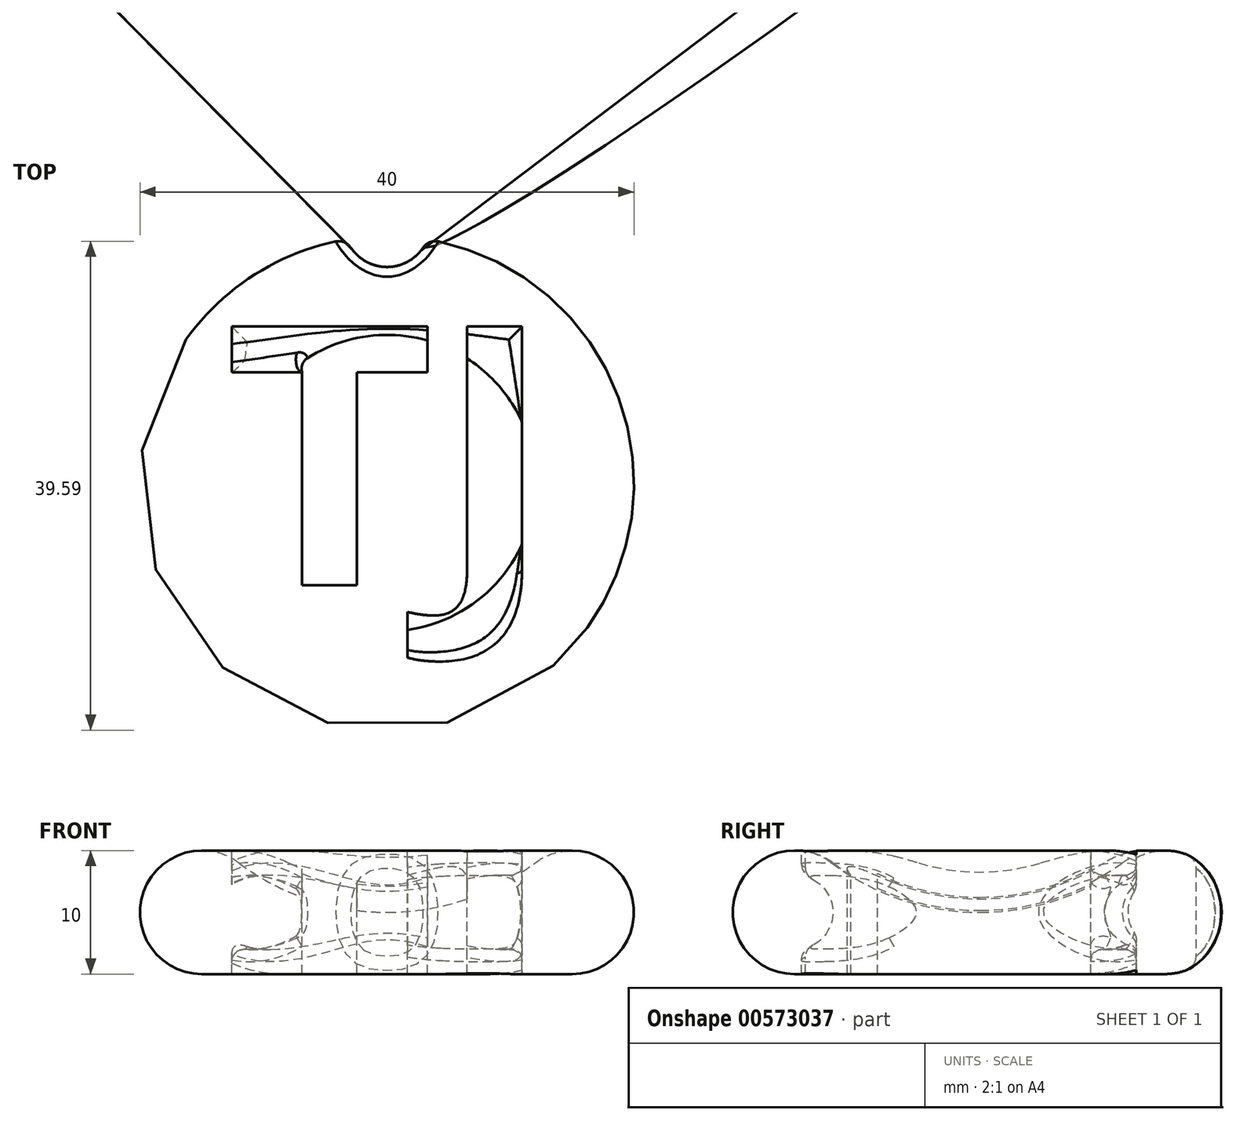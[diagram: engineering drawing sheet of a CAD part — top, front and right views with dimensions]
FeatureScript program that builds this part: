
annotation { "Feature Type Name" : "Feature", "Feature Type Description" : "" }
export const myFeature = defineFeature(function(context is Context, id is Id, definition is map)
    precondition{}
    {
        {
            var Q0;
            Q0=qCreatedBy(makeId("Front.planeOp"),FACE);
            var sketch = newSketch(context, id + "F0", { "sketchPlane" : qUnion([Q0])});
            skArc(sketch, "E0", {"start": v(-12, 9) * mm, "mid": v(-19.74, 6.58) * mm, "end": v(-15, 0) * mm});
            skArc(sketch, "E1", {"start": v(-12, 9) * mm, "mid": v(-6.32, 6.03) * mm, "end": v(0, 5) * mm});
            skLineSegment(sketch, "E2", {"start": v(0, 0) * mm, "end": v(-15, 0) * mm});
            skLineSegment(sketch, "E3", {"start": v(0, 0) * mm, "end": v(0, 5) * mm});
            skSolve(sketch);
        }
        {
            var Q0;
            Q0=makeQuery(id+"F0.imprint","IMPRINT",FACE,{"disambiguationData":[TD([[makeQuery(id+"F0.imprint","IMPRINT",EDGE,{"derivedFrom":sQuery(id+"F0.wireOp",EDGE,"E0")}),1.0]])]});
            var Q1;
            Q1=sQuery(id+"F0.wireOp",EDGE,"E3");
            revolve(context, id + "F1", {"entities" : qUnion([Q0]), "axis" : qUnion([Q1]), "revolveType" : RevolveType.FULL});
        }
        {
            var Q0;
            Q0=qCreatedBy(makeId("Top.planeOp"),FACE);
            cPlane(context, id + "F2", {"entities" : qUnion([Q0]), "cplaneType" : CPlaneType.OFFSET, "offset" : 11 * mm, "width" : 150 * mm, "height" : 150 * mm});
        }
        {
            var Q0;
            Q0=qCreatedBy(id+"F2.planeOp",FACE);
            var sketch = newSketch(context, id + "F3", { "sketchPlane" : qUnion([Q0])});
            skText(sketch, "E4", { "text": "TJ", "fontName": "OpenSans-Bold.ttf"});
            const initialGuessF3  = {"E4": [-0.01315, -0.00828, 1, 0, 0.02114]};
            skSetInitialGuess(sketch, initialGuessF3);
            skSolve(sketch);
        }
        {
            var Q0;
            Q0=makeQuery(id+"F3.imprint","IMPRINT",FACE,{"disambiguationData":[TD([[makeQuery(id+"F3.imprint","IMPRINT",EDGE,{"derivedFrom":sQuery(id+"F3.wireOp",EDGE,"E4.sketch_text.stroke-0")}),-1.0]])]});
            var Q1;
            Q1=makeQuery(id+"F3.imprint","IMPRINT",FACE,{"disambiguationData":[TD([[makeQuery(id+"F3.imprint","IMPRINT",EDGE,{"derivedFrom":sQuery(id+"F3.wireOp",EDGE,"E4.sketch_text.stroke-8")}),-1.0]])]});
            extrude(context, id + "F4", {"entities" : qUnion([Q0, Q1]), "operationType" : NewBodyOperationType.REMOVE, "endBound" : BoundingType.THROUGH_ALL, "oppositeDirection" : true, "depth" : 25 * mm, "offsetDistance" : 25 * mm});
        }
        {
            var Q0;
            Q0=qCreatedBy(makeId("Front.planeOp"),FACE);
            var sketch = newSketch(context, id + "F5", { "sketchPlane" : qUnion([Q0])});
            skCircle(sketch, "E5", {"center": v(-15, 5) * mm, "radius": 3 * mm});
            skSolve(sketch);
        }
        {
            var Q0;
            Q0 = qSketchRegion(id + "F5", true);
            var Q1;
            Q1=sQuery(id+"F0.wireOp",EDGE,"E3");
            revolve(context, id + "F6", {"operationType" : NewBodyOperationType.ADD, "entities" : qUnion([Q0]), "axis" : qUnion([Q1]), "revolveType" : RevolveType.FULL});
        }
        {
            var Q0;
            Q0=qCreatedBy(makeId("Top.planeOp"),FACE);
            var sketch = newSketch(context, id + "F7", { "sketchPlane" : qUnion([Q0])});
            skCircle(sketch, "E6", {"center": v(0, 21) * mm, "radius": 3.5 * mm});
            skSolve(sketch);
        }
        {
            var Q0;
            Q0 = qSketchRegion(id + "F7", true);
            extrude(context, id + "F8", {"entities" : qUnion([Q0]), "operationType" : NewBodyOperationType.REMOVE, "endBound" : BoundingType.THROUGH_ALL, "depth" : 25 * mm, "offsetDistance" : 25 * mm});
        }
        {
            var Q0;
            Q0=makeQuery(id+"F8.boolean.opBoolean","INTERSECT",EDGE,{"derivedFrom":[makeQuery(id+"F1.opRevolve","SWEPT_FACE",FACE,{"disambiguationData":[OSD([sQuery(id+"F0.wireOp",EDGE,"E0")])]}),makeQuery(id+"F8.opExtrude","SWEPT_FACE",FACE,{"disambiguationData":[OSD([sQuery(id+"F7.wireOp",EDGE,"E6")])]})]});
            fillet(context, id + "F9", {"entities" : qUnion([Q0]), "radius" : 1.2 * mm, "tangentPropagation" : true, "allowEdgeOverflow" : false});
        }
        {
            var Q0;
            Q0=makeQuery(id+"F6.boolean.opBoolean","INTERSECT",EDGE,{"disambiguationData":[OD(0.0)],"derivedFrom":[makeQuery(id+"F4.boolean.opBoolean","COPY",FACE,{"derivedFrom":makeQuery(id+"F4.opExtrude","SWEPT_FACE",FACE,{"disambiguationData":[OSD([sQuery(id+"F3.wireOp",EDGE,"E4.sketch_text.stroke-4")])]})}),makeQuery(id+"F6.opRevolve","SWEPT_FACE",FACE,{"disambiguationData":[OSD([sQuery(id+"F5.wireOp",EDGE,"E5")])]})]});
            var Q1;
            Q1=makeQuery(id+"F6.boolean.opBoolean","INTERSECT",EDGE,{"disambiguationData":[OD(0.0)],"derivedFrom":[makeQuery(id+"F4.boolean.opBoolean","COPY",FACE,{"derivedFrom":makeQuery(id+"F4.opExtrude","SWEPT_FACE",FACE,{"disambiguationData":[OSD([sQuery(id+"F3.wireOp",EDGE,"E4.sketch_text.stroke-14")])]})}),makeQuery(id+"F6.opRevolve","SWEPT_FACE",FACE,{"disambiguationData":[OSD([sQuery(id+"F5.wireOp",EDGE,"E5")])]})]});
            var Q2;
            Q2=makeQuery(id+"F6.boolean.opBoolean","INTERSECT",EDGE,{"disambiguationData":[OD(1.0)],"derivedFrom":[makeQuery(id+"F4.boolean.opBoolean","COPY",FACE,{"derivedFrom":makeQuery(id+"F4.opExtrude","SWEPT_FACE",FACE,{"disambiguationData":[OSD([sQuery(id+"F3.wireOp",EDGE,"E4.sketch_text.stroke-17")])]})}),makeQuery(id+"F6.opRevolve","SWEPT_FACE",FACE,{"disambiguationData":[OSD([sQuery(id+"F5.wireOp",EDGE,"E5")])]})]});
            var Q3;
            Q3=makeQuery(id+"F6.boolean.opBoolean","INTERSECT",EDGE,{"derivedFrom":[makeQuery(id+"F4.boolean.opBoolean","COPY",FACE,{"derivedFrom":makeQuery(id+"F4.opExtrude","SWEPT_FACE",FACE,{"disambiguationData":[OSD([sQuery(id+"F3.wireOp",EDGE,"E4.sketch_text.stroke-2")])]})}),makeQuery(id+"F6.opRevolve","SWEPT_FACE",FACE,{"disambiguationData":[OSD([sQuery(id+"F5.wireOp",EDGE,"E5")])]})]});
            var Q4;
            Q4=makeQuery(id+"F6.boolean.opBoolean","INTERSECT",EDGE,{"disambiguationData":[OD(1.0)],"derivedFrom":[makeQuery(id+"F4.boolean.opBoolean","COPY",FACE,{"derivedFrom":makeQuery(id+"F4.opExtrude","SWEPT_FACE",FACE,{"disambiguationData":[OSD([sQuery(id+"F3.wireOp",EDGE,"E4.sketch_text.stroke-4")])]})}),makeQuery(id+"F6.opRevolve","SWEPT_FACE",FACE,{"disambiguationData":[OSD([sQuery(id+"F5.wireOp",EDGE,"E5")])]})]});
            var Q5;
            Q5=makeQuery(id+"F6.boolean.opBoolean","INTERSECT",EDGE,{"disambiguationData":[OD(1.0)],"derivedFrom":[makeQuery(id+"F4.boolean.opBoolean","COPY",FACE,{"derivedFrom":makeQuery(id+"F4.opExtrude","SWEPT_FACE",FACE,{"disambiguationData":[OSD([sQuery(id+"F3.wireOp",EDGE,"E4.sketch_text.stroke-3")])]})}),makeQuery(id+"F6.opRevolve","SWEPT_FACE",FACE,{"disambiguationData":[OSD([sQuery(id+"F5.wireOp",EDGE,"E5")])]})]});
            var Q6;
            Q6=makeQuery(id+"F6.boolean.opBoolean","INTERSECT",EDGE,{"disambiguationData":[OD(0.0)],"derivedFrom":[makeQuery(id+"F4.boolean.opBoolean","COPY",FACE,{"derivedFrom":makeQuery(id+"F4.opExtrude","SWEPT_FACE",FACE,{"disambiguationData":[OSD([sQuery(id+"F3.wireOp",EDGE,"E4.sketch_text.stroke-15")])]})}),makeQuery(id+"F6.opRevolve","SWEPT_FACE",FACE,{"disambiguationData":[OSD([sQuery(id+"F5.wireOp",EDGE,"E5")])]})]});
            var Q7;
            Q7=makeQuery(id+"F6.boolean.opBoolean","INTERSECT",EDGE,{"disambiguationData":[OD(1.0)],"derivedFrom":[makeQuery(id+"F4.boolean.opBoolean","COPY",FACE,{"derivedFrom":makeQuery(id+"F4.opExtrude","SWEPT_FACE",FACE,{"disambiguationData":[OSD([sQuery(id+"F3.wireOp",EDGE,"E4.sketch_text.stroke-14")])]})}),makeQuery(id+"F6.opRevolve","SWEPT_FACE",FACE,{"disambiguationData":[OSD([sQuery(id+"F5.wireOp",EDGE,"E5")])]})]});
            fillet(context, id + "F10", {"entities" : qUnion([Q0, Q1, Q2, Q3, Q4, Q5, Q6, Q7]), "radius" : 1 * mm, "tangentPropagation" : true, "allowEdgeOverflow" : false});
        }
    });
